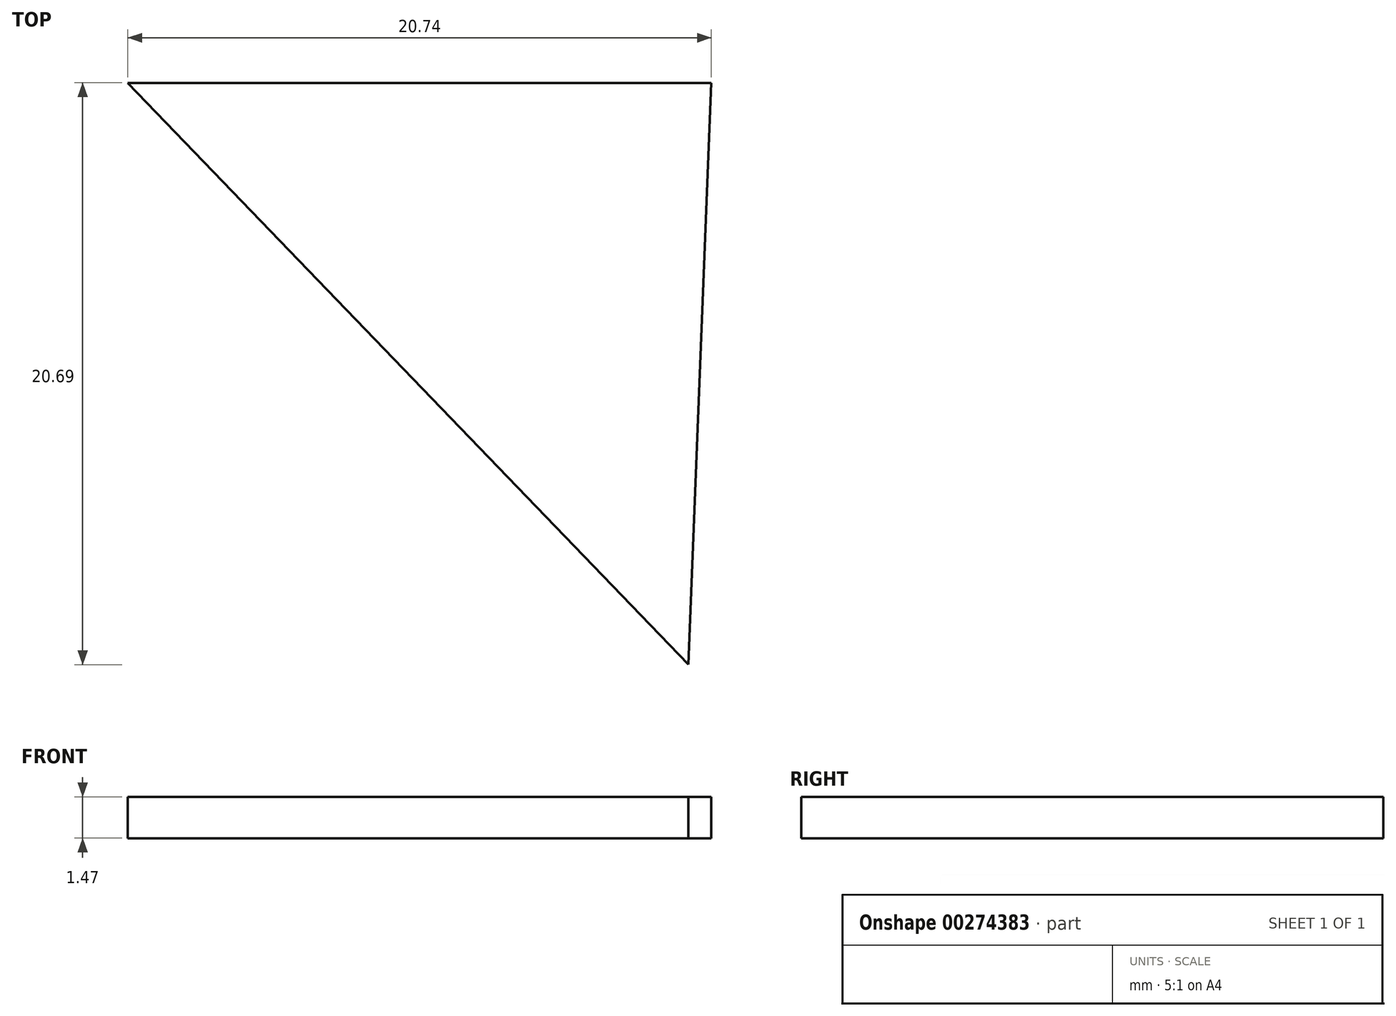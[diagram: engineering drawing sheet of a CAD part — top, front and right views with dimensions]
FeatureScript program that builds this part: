
annotation { "Feature Type Name" : "Feature", "Feature Type Description" : "" }
export const myFeature = defineFeature(function(context is Context, id is Id, definition is map)
    precondition{}
    {
        {
            var Q0;
            Q0=qCreatedBy(makeId("Top.planeOp"),FACE);
            var sketch = newSketch(context, id + "F0", { "sketchPlane" : qUnion([Q0])});
            skLineSegment(sketch, "E0", {"start": v(-25.73, -40.99) * mm, "end": v(-24.92, -20.3) * mm});
            skLineSegment(sketch, "E1", {"start": v(-24.92, -20.3) * mm, "end": v(-45.66, -20.3) * mm});
            skLineSegment(sketch, "E2", {"start": v(-45.66, -20.3) * mm, "end": v(-25.73, -40.99) * mm});
            skSolve(sketch);
        }
        {
            var Q0;
            Q0=makeQuery(id+"F0.imprint","IMPRINT",FACE,{"disambiguationData":[TD([[makeQuery(id+"F0.imprint","IMPRINT",EDGE,{"derivedFrom":sQuery(id+"F0.wireOp",EDGE,"E0")}),1.0]])]});
            extrude(context, id + "F1", {"entities" : qUnion([Q0]), "oppositeDirection" : true, "depth" : 1.47 * mm});
        }
    });
